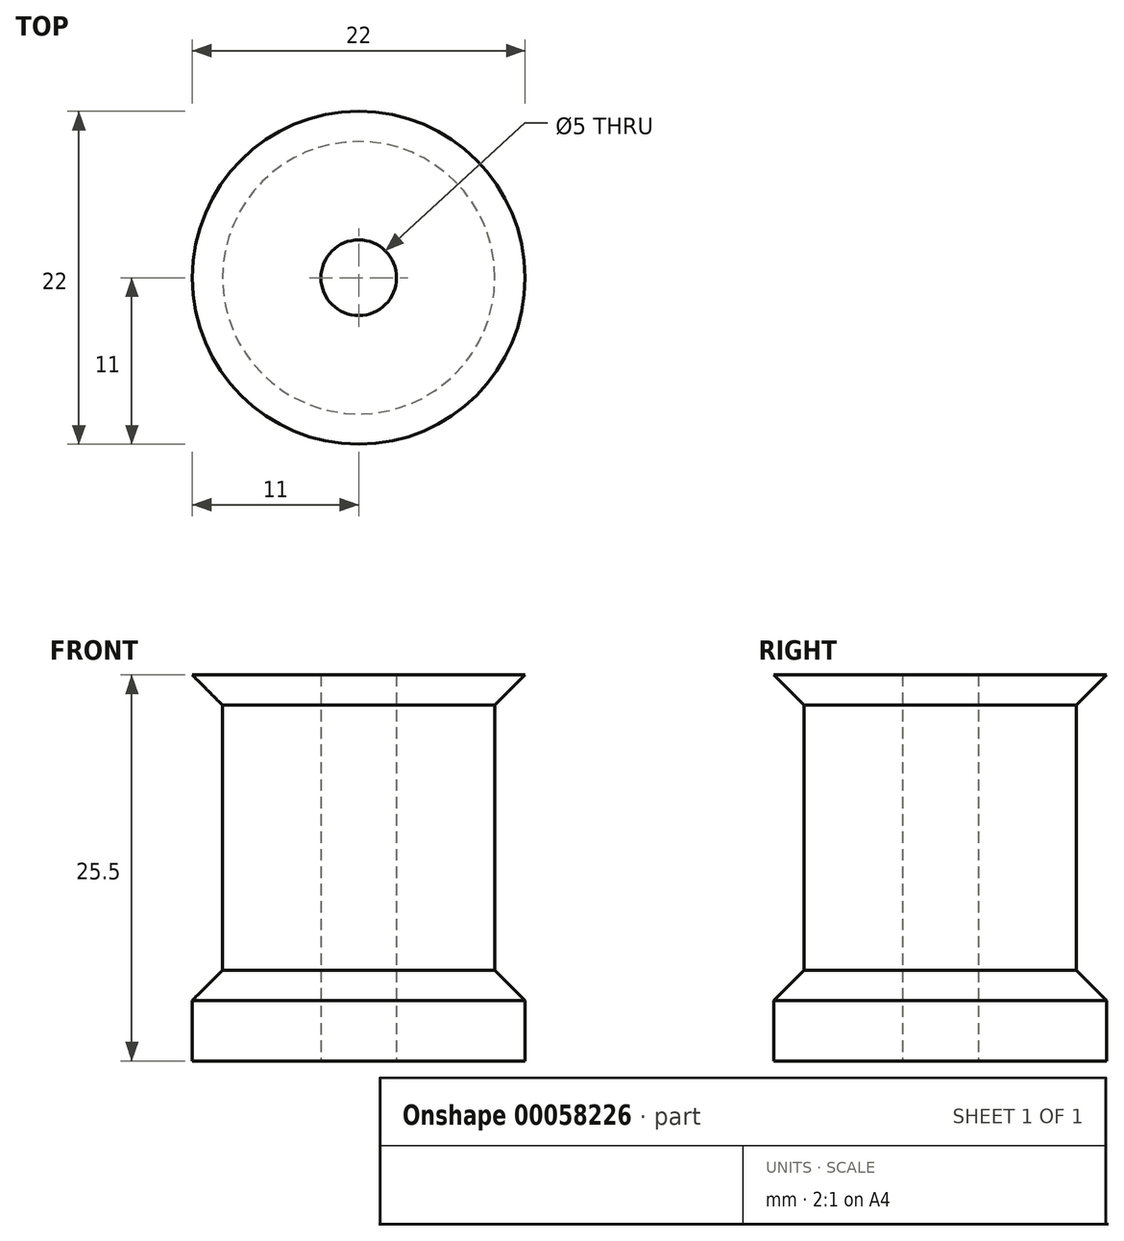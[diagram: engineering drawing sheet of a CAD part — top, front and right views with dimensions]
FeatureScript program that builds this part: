
annotation { "Feature Type Name" : "Feature", "Feature Type Description" : "" }
export const myFeature = defineFeature(function(context is Context, id is Id, definition is map)
    precondition{}
    {
        {
            var Q0;
            Q0=qCreatedBy(makeId("Front.planeOp"),FACE);
            var sketch = newSketch(context, id + "F0", { "sketchPlane" : qUnion([Q0])});
            skLineSegment(sketch, "E0", {"start": v(2.5, 0) * mm, "end": v(2.5, 25.5) * mm});
            skLineSegment(sketch, "E1", {"start": v(2.5, 25.5) * mm, "end": v(11, 25.5) * mm});
            skLineSegment(sketch, "E2", {"start": v(11, 25.5) * mm, "end": v(9, 23.5) * mm});
            skLineSegment(sketch, "E3", {"start": v(9, 23.5) * mm, "end": v(9, 6) * mm});
            skLineSegment(sketch, "E4", {"start": v(9, 6) * mm, "end": v(11, 4) * mm});
            skLineSegment(sketch, "E5", {"start": v(11, 4) * mm, "end": v(11, 0) * mm});
            skLineSegment(sketch, "E6", {"start": v(11, 0) * mm, "end": v(2.5, 0) * mm});
            skLineSegment(sketch, "E7", {"start": v(0, 0) * mm, "end": v(0, 36.43) * mm, "construction": true});
            skSolve(sketch);
        }
        {
            var Q0;
            Q0 = qSketchRegion(id + "F0", true);
            var Q1;
            Q1=sQuery(id+"F0.wireOp",EDGE,"E7");
            revolve(context, id + "F1", {"entities" : qUnion([Q0]), "axis" : qUnion([Q1]), "revolveType" : RevolveType.FULL});
        }
    });
